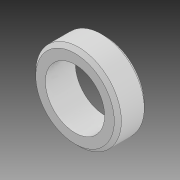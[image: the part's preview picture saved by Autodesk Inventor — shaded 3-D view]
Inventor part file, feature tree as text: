
AUTODESK INVENTOR PART (.ipt)
format: ipt  version: 2020 (Build 240168000, 168)  size: 99,840 bytes
history: native  units: mm
features: extrude x1, chamfer x1, sketch x1
ambient origin geometry x8: Origin, YZ Plane, XZ Plane, XY Plane, X Axis, Y Axis, Z Axis, Center Point
bodies: Solid1 (feature_tree)
feature tree (3):
  extrude  "Extrusion1"  Depth=4.2mm
  chamfer  "Chamfer1"  Distance=4.2mm
  sketch  "Sketch1"  dims[d0=8.3mm d1=12.0mm d2=4.2mm d3=0.0mm d4=0.5mm d5=2.0mm d6=45.0deg]
